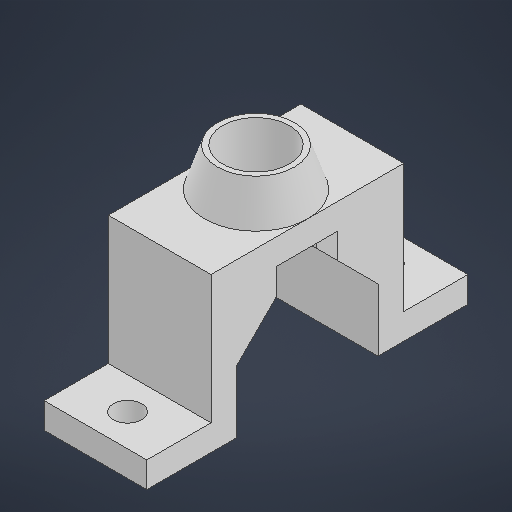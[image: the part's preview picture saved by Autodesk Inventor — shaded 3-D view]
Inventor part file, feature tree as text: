
AUTODESK INVENTOR PART (.ipt)
format: ipt  version: 2025.1 (Build 291241000, 241)  size: 515,584 bytes
history: native  units: mm
features: extrude x5, chamfer x2, sketch x1
ambient origin geometry x8: Origin, YZ Plane, XZ Plane, XY Plane, X Axis, Y Axis, Z Axis, Center Point
bodies: Solid1 (feature_tree)
feature tree (8):
  sketch  "Sketch1"  dims[d0=20.0mm d1=2.2mm d2=8.0mm d3=15.0mm d4=5.0mm d5=2.0mm d6=2.0mm d7=5.2mm d8=2.0mm d9=0.0mm d10=10.0mm d11=0.0mm d12=2.0mm d13=0.0mm d14=8.1mm d15=2.0mm d16=0.0mm d17=6.0mm d18=3.0mm d19=0.0mm d20=1.0mm d21=3.0mm d22=45.0deg d26=3.13mm d27=2.0mm d28=45.0deg]
  extrude  "Extrusion1"  Depth=2.0mm
  extrude  "Extrusion2"  Depth=8.0mm
  extrude  "Extrusion3"  Depth=15.0mm
  extrude  "Extrusion4"  Depth=5.0mm
  extrude  "Extrusion5"  Depth=2.0mm
  chamfer  "Chamfer1"  Distance=2.0mm
  chamfer  "Chamfer3"  Distance=5.2mm
